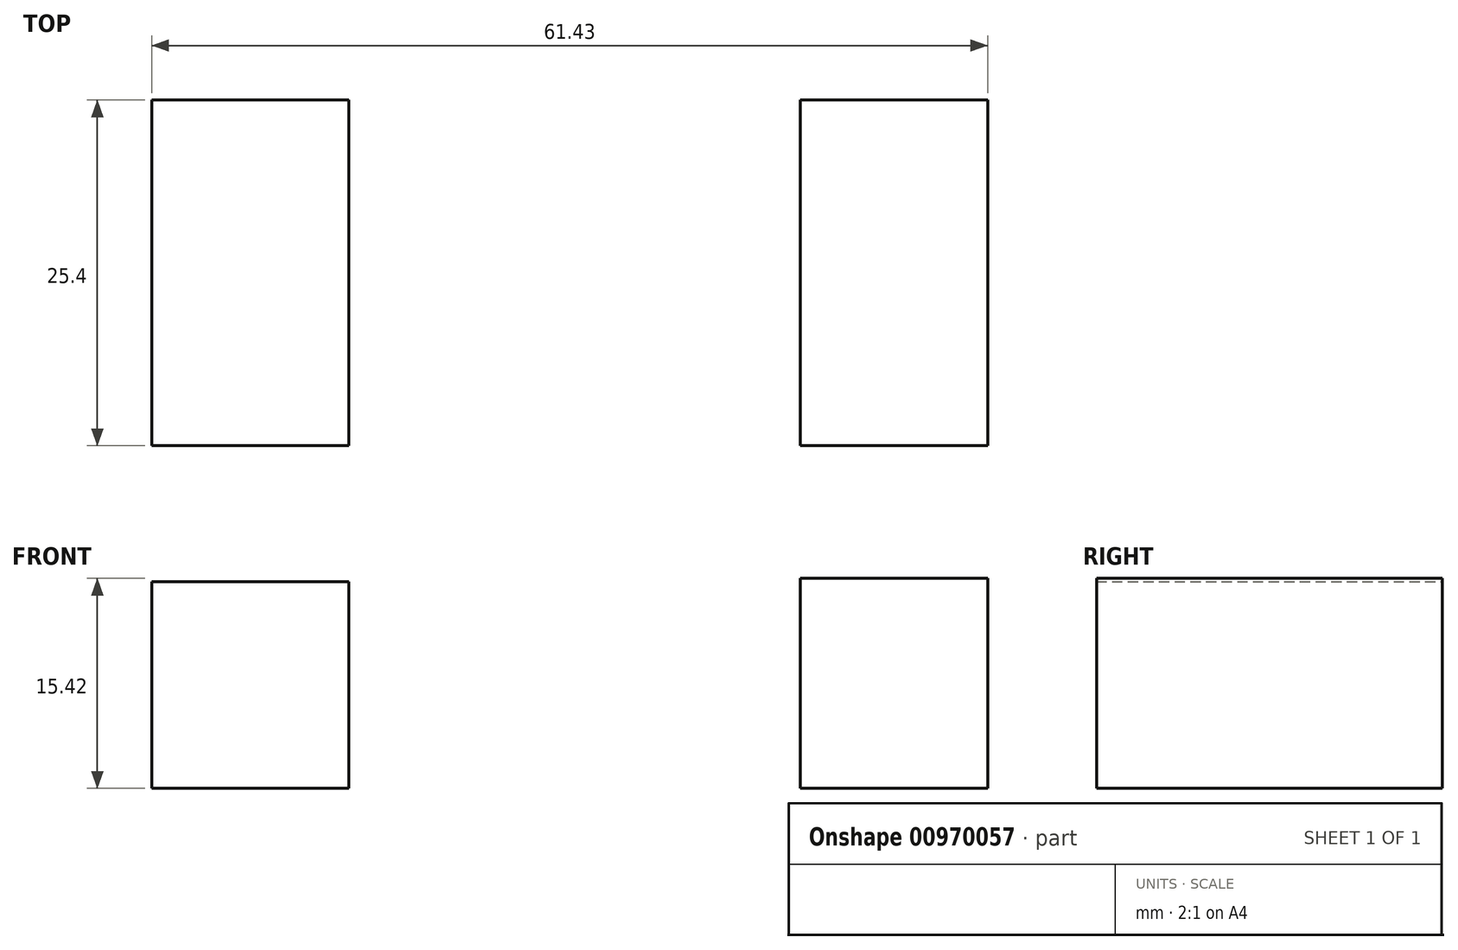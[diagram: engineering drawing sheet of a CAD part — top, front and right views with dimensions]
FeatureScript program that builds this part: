
annotation { "Feature Type Name" : "Feature", "Feature Type Description" : "" }
export const myFeature = defineFeature(function(context is Context, id is Id, definition is map)
    precondition{}
    {
        {
            var Q0;
            Q0=qCreatedBy(makeId("Front.planeOp"),FACE);
            var sketch = newSketch(context, id + "F0", { "sketchPlane" : qUnion([Q0])});
            skLineSegment(sketch, "E0.bottom", {"start": v(-61.43, 0) * mm, "end": v(-46.95, 0) * mm});
            skLineSegment(sketch, "E0.top", {"start": v(-61.43, 15.18) * mm, "end": v(-46.95, 15.18) * mm});
            skLineSegment(sketch, "E0.left", {"start": v(-61.43, 0) * mm, "end": v(-61.43, 15.18) * mm});
            skLineSegment(sketch, "E0.right", {"start": v(-46.95, 0) * mm, "end": v(-46.95, 15.18) * mm});
            skLineSegment(sketch, "E1.bottom", {"start": v(0, 0) * mm, "end": v(-13.78, 0) * mm});
            skLineSegment(sketch, "E1.top", {"start": v(0, 15.42) * mm, "end": v(-13.78, 15.42) * mm});
            skLineSegment(sketch, "E1.left", {"start": v(0, 0) * mm, "end": v(0, 15.42) * mm});
            skLineSegment(sketch, "E1.right", {"start": v(-13.78, 0) * mm, "end": v(-13.78, 15.42) * mm});
            skSolve(sketch);
        }
        {
            var Q0;
            Q0 = qSketchRegion(id + "F0", true);
            extrude(context, id + "F1", {"entities" : qUnion([Q0]), "depth" : 25.4 * mm, "offsetDistance" : 25.4 * mm});
        }
    });
